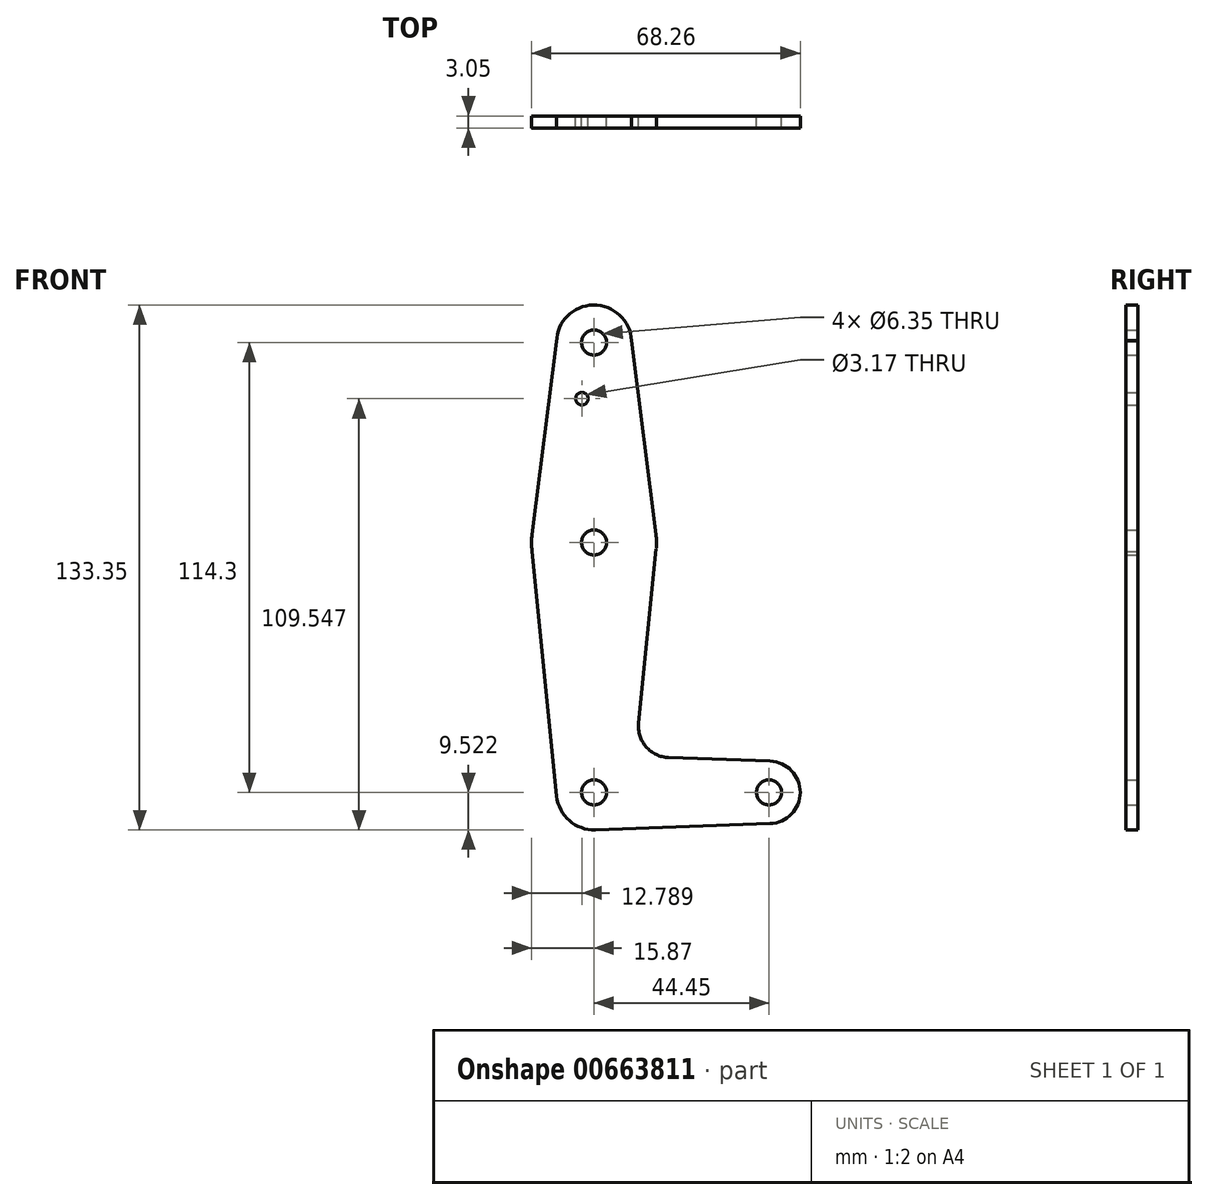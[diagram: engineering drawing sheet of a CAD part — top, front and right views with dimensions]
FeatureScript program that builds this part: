
annotation { "Feature Type Name" : "Feature", "Feature Type Description" : "" }
export const myFeature = defineFeature(function(context is Context, id is Id, definition is map)
    precondition{}
    {
        {
            var Q0;
            Q0=qCreatedBy(makeId("Front.planeOp"),FACE);
            var sketch = newSketch(context, id + "F0", { "sketchPlane" : qUnion([Q0])});
            skLineSegment(sketch, "E0", {"start": v(0, 56.53) * mm, "end": v(0, -57.77) * mm, "construction": true});
            skLineSegment(sketch, "E1", {"start": v(0, -57.77) * mm, "end": v(44.45, -57.77) * mm, "construction": true});
            skCircle(sketch, "E2", {"center": v(0, 56.53) * mm, "radius": 9.53 * mm});
            skCircle(sketch, "E3", {"center": v(44.45, -57.77) * mm, "radius": 7.94 * mm});
            skCircle(sketch, "E4", {"center": v(0, 5.73) * mm, "radius": 15.88 * mm});
            skCircle(sketch, "E5", {"center": v(0, -57.77) * mm, "radius": 9.53 * mm});
            skLineSegment(sketch, "E6", {"start": v(-9.52, 56.76) * mm, "end": v(-15.75, 7.73) * mm});
            skLineSegment(sketch, "E7", {"start": v(9.51, 57.03) * mm, "end": v(15.75, 7.72) * mm});
            skLineSegment(sketch, "E8", {"start": v(-15.7, 3.4) * mm, "end": v(-9.48, -58.72) * mm});
            skLineSegment(sketch, "E9", {"start": v(15.8, 4.14) * mm, "end": v(11.32, -40.17) * mm});
            skLineSegment(sketch, "E10", {"start": v(18.95, -48.92) * mm, "end": v(44.73, -49.84) * mm});
            skLineSegment(sketch, "E11", {"start": v(0.34, -67.29) * mm, "end": v(44.73, -65.7) * mm});
            skCircle(sketch, "E12", {"center": v(0, 56.53) * mm, "radius": 3.18 * mm});
            skCircle(sketch, "E13", {"center": v(44.45, -57.77) * mm, "radius": 3.18 * mm});
            skCircle(sketch, "E14", {"center": v(0, -57.77) * mm, "radius": 3.18 * mm});
            skCircle(sketch, "E15", {"center": v(0, 5.73) * mm, "radius": 3.18 * mm});
            skCircle(sketch, "E16", {"center": v(-3.08, 42.26) * mm, "radius": 1.59 * mm});
            skArc(sketch, "E17.filletArc", {"start": v(11.32, -40.17) * mm, "mid": v(13.24, -46.2) * mm, "end": v(18.95, -48.92) * mm});
            skSolve(sketch);
        }
        {
            var Q0;
            Q0 = qSketchRegion(id + "F0", true);
            extrude(context, id + "F1", {"entities" : qUnion([Q0]), "depth" : 3.05 * mm, "offsetDistance" : 25.4 * mm});
        }
    });
